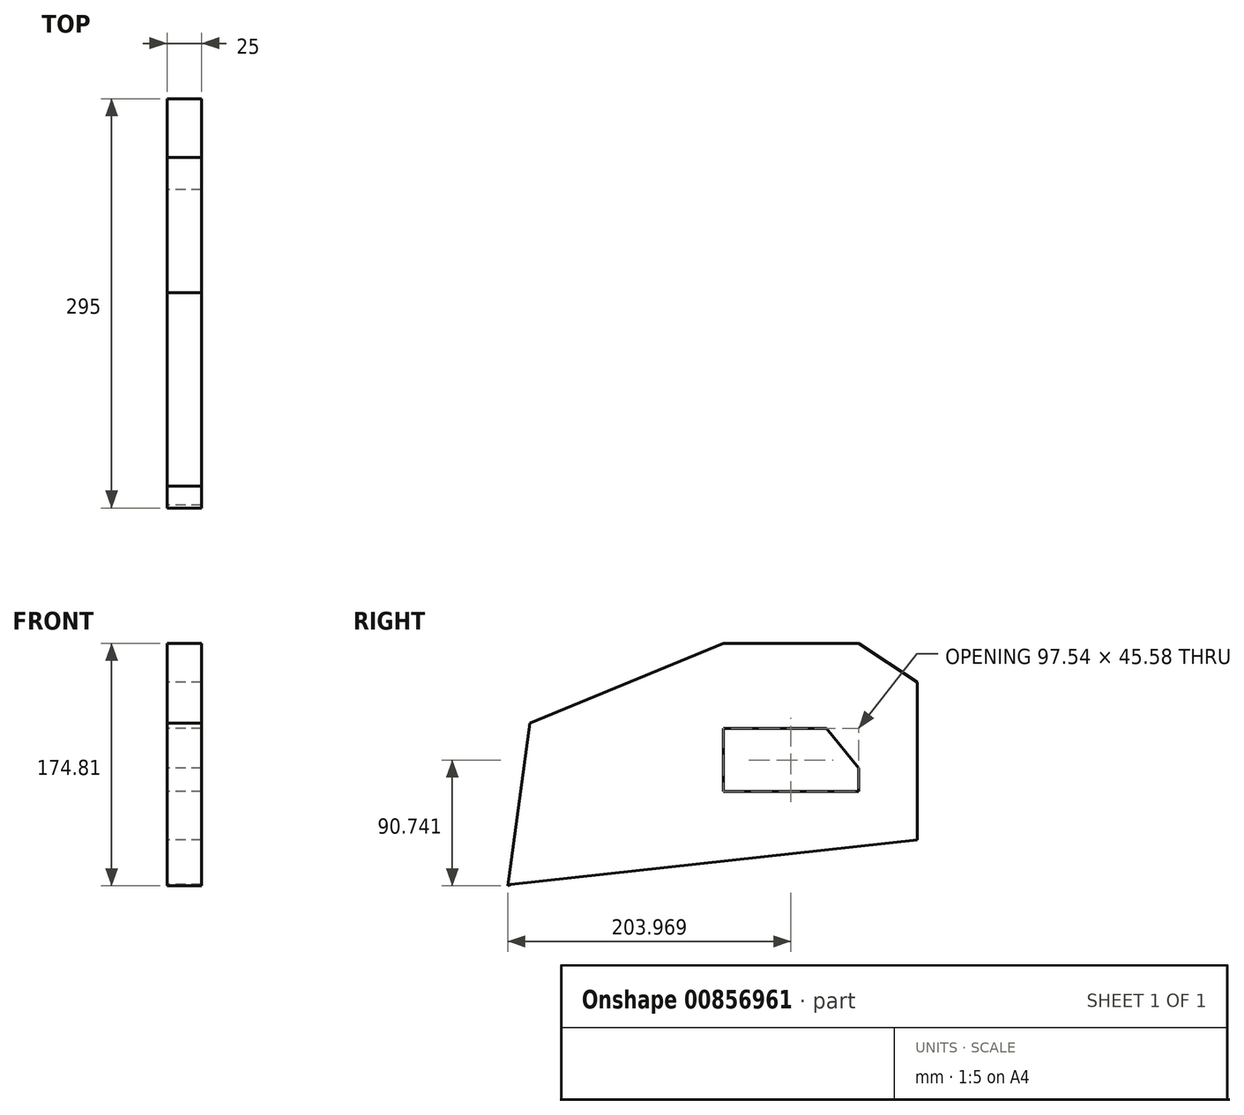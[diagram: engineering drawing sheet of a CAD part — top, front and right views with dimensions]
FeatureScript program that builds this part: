
annotation { "Feature Type Name" : "Feature", "Feature Type Description" : "" }
export const myFeature = defineFeature(function(context is Context, id is Id, definition is map)
    precondition{}
    {
        {
            var Q0;
            Q0=qCreatedBy(makeId("Right.planeOp"),FACE);
            var sketch = newSketch(context, id + "F0", { "sketchPlane" : qUnion([Q0])});
            skLineSegment(sketch, "E0", {"start": v(47.37, 49.08) * mm, "end": v(-46.75, 49.08) * mm});
            skLineSegment(sketch, "E1", {"start": v(-46.75, 49.08) * mm, "end": v(-46.75, -57.78) * mm});
            skLineSegment(sketch, "E2", {"start": v(-46.75, -57.78) * mm, "end": v(50.8, -57.78) * mm});
            skLineSegment(sketch, "E3", {"start": v(50.8, -57.78) * mm, "end": v(50.8, 49.08) * mm});
            skLineSegment(sketch, "E4", {"start": v(50.8, 49.08) * mm, "end": v(47.37, 49.08) * mm});
            skLineSegment(sketch, "E5", {"start": v(-46.75, -57.78) * mm, "end": v(-201.95, -125.73) * mm});
            skLineSegment(sketch, "E6", {"start": v(-201.95, -125.73) * mm, "end": v(-186.2, -8.4) * mm});
            skLineSegment(sketch, "E7", {"start": v(-186.2, -8.4) * mm, "end": v(-46.75, 49.08) * mm});
            skLineSegment(sketch, "E8", {"start": v(50.8, 49.08) * mm, "end": v(93.05, 21.07) * mm});
            skLineSegment(sketch, "E9", {"start": v(93.05, 21.07) * mm, "end": v(93.05, -92.73) * mm});
            skLineSegment(sketch, "E10", {"start": v(93.05, -92.73) * mm, "end": v(50.8, -57.78) * mm});
            skLineSegment(sketch, "E11", {"start": v(-208.64, -125.73) * mm, "end": v(93.05, -92.73) * mm});
            skLineSegment(sketch, "E12", {"start": v(-186.71, -12.2) * mm, "end": v(27.64, -12.2) * mm});
            skLineSegment(sketch, "E13", {"start": v(27.64, -12.2) * mm, "end": v(93.05, -92.73) * mm});
            skLineSegment(sketch, "E14", {"start": v(50.8, 49.08) * mm, "end": v(27.64, -12.2) * mm});
            skSolve(sketch);
        }
        {
            var Q0;
            Q0 = qSketchRegion(id + "F0", true);
            extrude(context, id + "F1", {"entities" : qUnion([Q0]), "depth" : 25 * mm, "offsetDistance" : 25 * mm});
        }
    });
